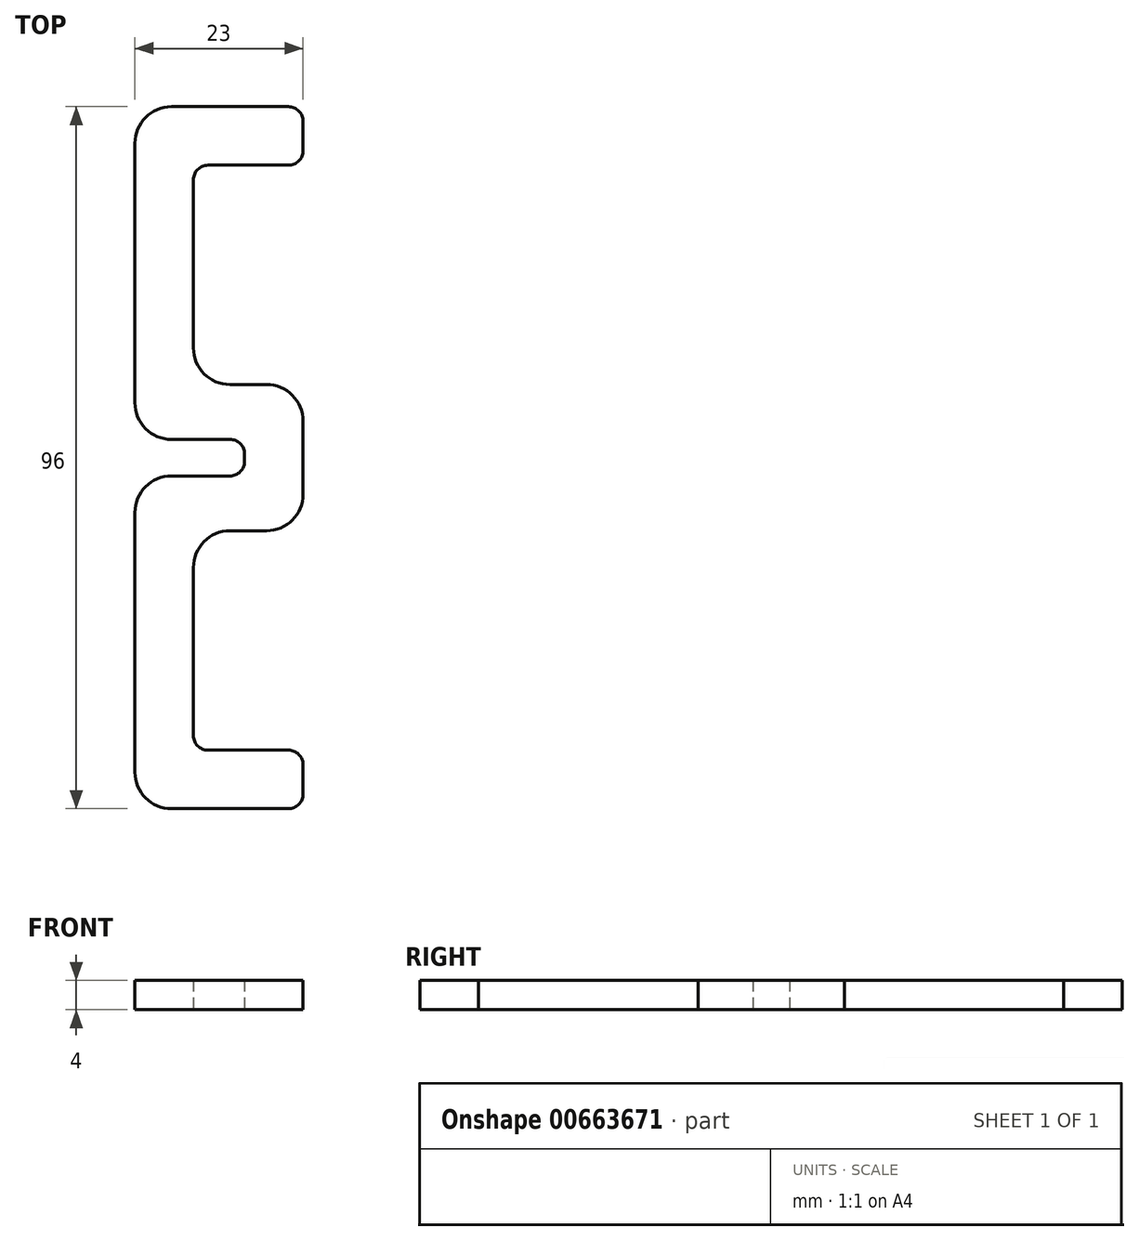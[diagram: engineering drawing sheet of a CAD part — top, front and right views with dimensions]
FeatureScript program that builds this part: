
annotation { "Feature Type Name" : "Feature", "Feature Type Description" : "" }
export const myFeature = defineFeature(function(context is Context, id is Id, definition is map)
    precondition{}
    {
        {
            var Q0;
            Q0=qCreatedBy(makeId("Top.planeOp"),FACE);
            var sketch = newSketch(context, id + "F0", { "sketchPlane" : qUnion([Q0])});
            skLineSegment(sketch, "E0", {"start": v(8.24, 48) * mm, "end": v(-7.76, 48) * mm});
            skLineSegment(sketch, "E1", {"start": v(-12.76, 43) * mm, "end": v(-12.76, 7.5) * mm});
            skLineSegment(sketch, "E2", {"start": v(-7.76, 2.5) * mm, "end": v(0.24, 2.5) * mm});
            skLineSegment(sketch, "E3", {"start": v(2.24, 0.5) * mm, "end": v(2.24, -0.5) * mm});
            skLineSegment(sketch, "E4", {"start": v(0.24, -2.5) * mm, "end": v(-7.76, -2.5) * mm});
            skLineSegment(sketch, "E5", {"start": v(-12.76, -7.5) * mm, "end": v(-12.76, -43) * mm});
            skLineSegment(sketch, "E6", {"start": v(-7.76, -48) * mm, "end": v(8.24, -48) * mm});
            skLineSegment(sketch, "E7", {"start": v(10.24, -46) * mm, "end": v(10.24, -42) * mm});
            skLineSegment(sketch, "E8", {"start": v(8.24, -40) * mm, "end": v(-2.76, -40) * mm});
            skLineSegment(sketch, "E9", {"start": v(-4.76, -38) * mm, "end": v(-4.76, -15) * mm});
            skLineSegment(sketch, "E10", {"start": v(0.24, -10) * mm, "end": v(5.24, -10) * mm});
            skLineSegment(sketch, "E11", {"start": v(10.24, -5) * mm, "end": v(10.24, 5) * mm});
            skLineSegment(sketch, "E12", {"start": v(5.24, 10) * mm, "end": v(0.24, 10) * mm});
            skLineSegment(sketch, "E13", {"start": v(-4.76, 15) * mm, "end": v(-4.76, 38) * mm});
            skLineSegment(sketch, "E14", {"start": v(-2.76, 40) * mm, "end": v(8.24, 40) * mm});
            skLineSegment(sketch, "E15", {"start": v(10.24, 42) * mm, "end": v(10.24, 46) * mm});
            skPoint(sketch, "E16.visualSharp", {"position": v(-12.76, 48) * mm});
            skArc(sketch, "E16.filletArc", {"start": v(-7.76, 48) * mm, "mid": v(-11.3, 46.54) * mm, "end": v(-12.76, 43) * mm});
            skPoint(sketch, "E17.visualSharp", {"position": v(-12.76, -48) * mm});
            skArc(sketch, "E17.filletArc", {"start": v(-12.76, -43) * mm, "mid": v(-11.3, -46.54) * mm, "end": v(-7.76, -48) * mm});
            skPoint(sketch, "E18.visualSharp", {"position": v(-12.76, -2.5) * mm});
            skArc(sketch, "E18.filletArc", {"start": v(-7.76, -2.5) * mm, "mid": v(-11.3, -3.96) * mm, "end": v(-12.76, -7.5) * mm});
            skPoint(sketch, "E19.visualSharp", {"position": v(-4.76, -10) * mm});
            skArc(sketch, "E19.filletArc", {"start": v(0.24, -10) * mm, "mid": v(-3.3, -11.46) * mm, "end": v(-4.76, -15) * mm});
            skPoint(sketch, "E20.visualSharp", {"position": v(10.24, -10) * mm});
            skArc(sketch, "E20.filletArc", {"start": v(5.24, -10) * mm, "mid": v(8.77, -8.54) * mm, "end": v(10.24, -5) * mm});
            skPoint(sketch, "E21.visualSharp", {"position": v(10.24, 10) * mm});
            skArc(sketch, "E21.filletArc", {"start": v(10.24, 5) * mm, "mid": v(8.77, 8.54) * mm, "end": v(5.24, 10) * mm});
            skPoint(sketch, "E22.visualSharp", {"position": v(-12.76, 2.5) * mm});
            skArc(sketch, "E22.filletArc", {"start": v(-12.76, 7.5) * mm, "mid": v(-11.3, 3.96) * mm, "end": v(-7.76, 2.5) * mm});
            skPoint(sketch, "E23.visualSharp", {"position": v(-4.76, 10) * mm});
            skArc(sketch, "E23.filletArc", {"start": v(-4.76, 15) * mm, "mid": v(-3.3, 11.46) * mm, "end": v(0.24, 10) * mm});
            skPoint(sketch, "E24.visualSharp", {"position": v(2.24, 2.5) * mm});
            skArc(sketch, "E24.filletArc", {"start": v(2.24, 0.5) * mm, "mid": v(1.65, 1.91) * mm, "end": v(0.24, 2.5) * mm});
            skPoint(sketch, "E25.visualSharp", {"position": v(2.24, -2.5) * mm});
            skArc(sketch, "E25.filletArc", {"start": v(0.24, -2.5) * mm, "mid": v(1.65, -1.91) * mm, "end": v(2.24, -0.5) * mm});
            skPoint(sketch, "E26.visualSharp", {"position": v(10.24, 40) * mm});
            skArc(sketch, "E26.filletArc", {"start": v(8.24, 40) * mm, "mid": v(9.65, 40.59) * mm, "end": v(10.24, 42) * mm});
            skPoint(sketch, "E27.visualSharp", {"position": v(10.24, 48) * mm});
            skArc(sketch, "E27.filletArc", {"start": v(10.24, 46) * mm, "mid": v(9.65, 47.41) * mm, "end": v(8.24, 48) * mm});
            skPoint(sketch, "E28.visualSharp", {"position": v(10.24, -48) * mm});
            skArc(sketch, "E28.filletArc", {"start": v(8.24, -48) * mm, "mid": v(9.65, -47.41) * mm, "end": v(10.24, -46) * mm});
            skPoint(sketch, "E29.visualSharp", {"position": v(10.24, -40) * mm});
            skArc(sketch, "E29.filletArc", {"start": v(10.24, -42) * mm, "mid": v(9.65, -40.59) * mm, "end": v(8.24, -40) * mm});
            skPoint(sketch, "E30.visualSharp", {"position": v(-4.76, -40) * mm});
            skArc(sketch, "E30.filletArc", {"start": v(-4.76, -38) * mm, "mid": v(-4.18, -39.41) * mm, "end": v(-2.76, -40) * mm});
            skPoint(sketch, "E31.visualSharp", {"position": v(-4.76, 40) * mm});
            skArc(sketch, "E31.filletArc", {"start": v(-2.76, 40) * mm, "mid": v(-4.18, 39.41) * mm, "end": v(-4.76, 38) * mm});
            skSolve(sketch);
        }
        {
            var Q0;
            Q0 = qSketchRegion(id + "F0", true);
            extrude(context, id + "F1", {"entities" : qUnion([Q0]), "depth" : 4 * mm, "offsetDistance" : 25 * mm});
        }
    });
